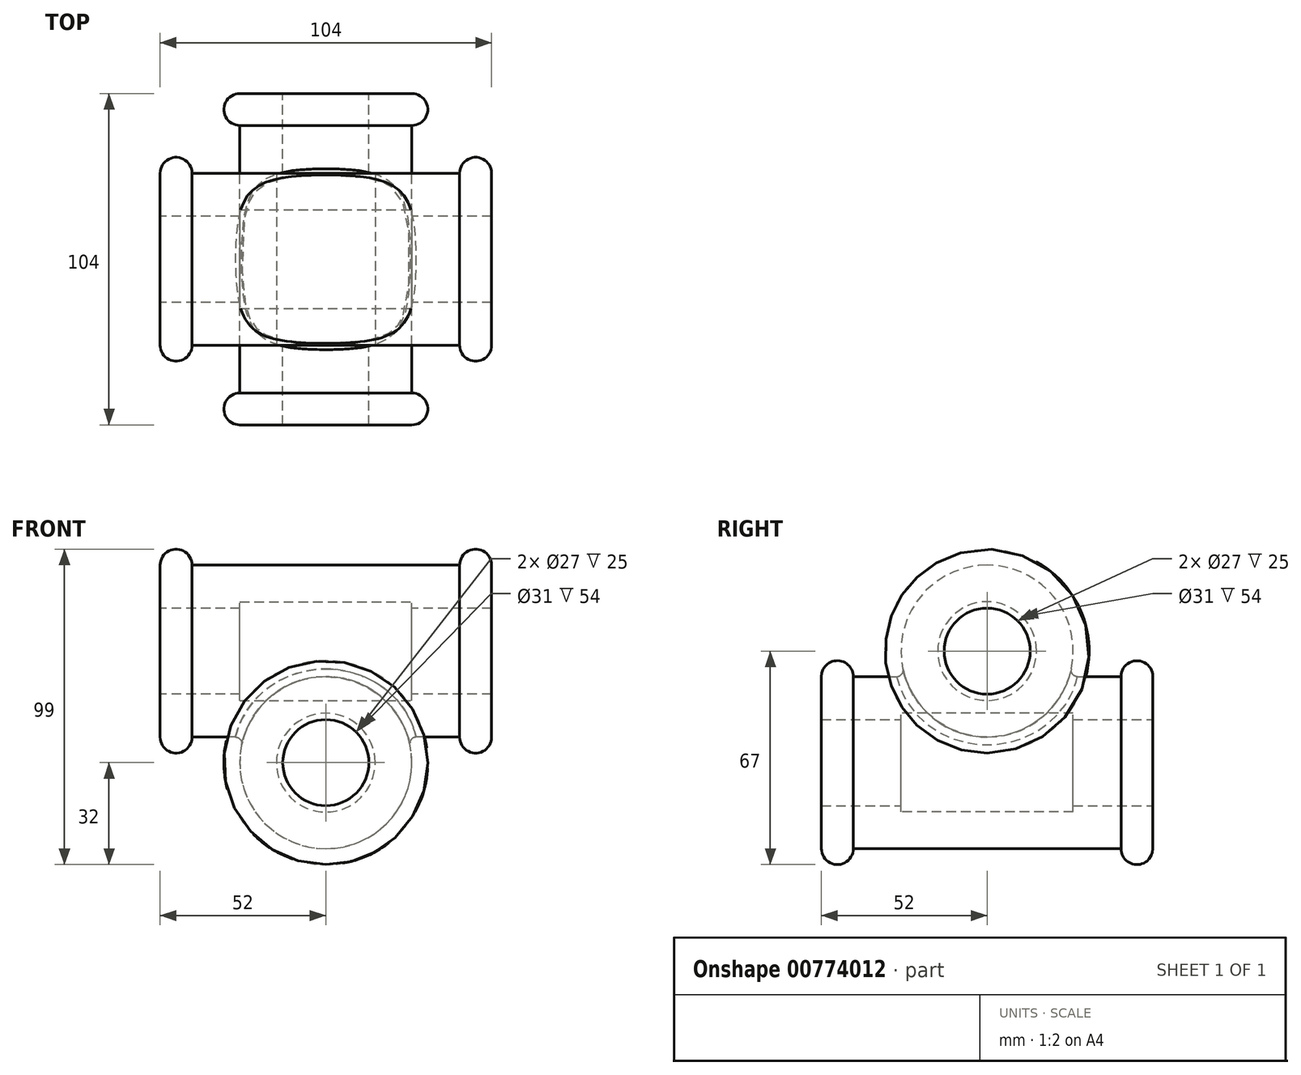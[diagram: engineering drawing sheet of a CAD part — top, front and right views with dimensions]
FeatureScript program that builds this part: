
annotation { "Feature Type Name" : "Feature", "Feature Type Description" : "" }
export const myFeature = defineFeature(function(context is Context, id is Id, definition is map)
    precondition{}
    {
        {
            var Q0;
            Q0=qCreatedBy(makeId("Front.planeOp"),FACE);
            var sketch = newSketch(context, id + "F0", { "sketchPlane" : qUnion([Q0])});
            skCircle(sketch, "E0", {"center": v(0, 0) * mm, "radius": 13.5 * mm});
            skCircle(sketch, "E1", {"center": v(0, 0) * mm, "radius": 15.5 * mm});
            skCircle(sketch, "E2", {"center": v(0, 0) * mm, "radius": 27 * mm});
            skSolve(sketch);
        }
        {
            var Q0;
            Q0 = qSketchRegion(id + "F0", true);
            var Q1;
            Q1=makeQuery(id+"F0.imprint","IMPRINT",FACE,{"disambiguationData":[TD([[makeQuery(id+"F0.imprint","IMPRINT",EDGE,{"derivedFrom":sQuery(id+"F0.wireOp",EDGE,"E0")}),-1.0]])]});
            extrude(context, id + "F1", {"entities" : qUnion([Q0, Q1]), "depth" : 104 * mm, "offsetDistance" : 25 * mm, "symmetric" : true});
        }
        {
            var Q0;
            Q0=makeQuery(id+"F1.opExtrude","CAP_FACE",FACE,{"disambiguationData":[OSD([sQuery(id+"F0.wireOp",EDGE,"E0"),sQuery(id+"F0.wireOp",EDGE,"E2")])],"isStart":true});
            var sketch = newSketch(context, id + "F2", { "sketchPlane" : qUnion([Q0])});
            skCircle(sketch, "E3", {"center": v(0, 0) * mm, "radius": 32 * mm});
            skSolve(sketch);
        }
        {
            var Q0;
            Q0=makeQuery(id+"F2.imprint","IMPRINT",FACE,{"disambiguationData":[TD([[makeQuery(id+"F2.imprint","IMPRINT",EDGE,{"derivedFrom":sQuery(id+"F2.wireOp",EDGE,"E3")}),1.0]])]});
            extrude(context, id + "F3", {"entities" : qUnion([Q0]), "operationType" : NewBodyOperationType.ADD, "oppositeDirection" : true, "depth" : 10 * mm, "offsetDistance" : 25 * mm});
        }
        {
            var Q0;
            Q0=makeQuery(id+"F1.opExtrude","CAP_FACE",FACE,{"disambiguationData":[OSD([sQuery(id+"F0.wireOp",EDGE,"E0"),sQuery(id+"F0.wireOp",EDGE,"E2")])],"isStart":false});
            var sketch = newSketch(context, id + "F4", { "sketchPlane" : qUnion([Q0])});
            skCircle(sketch, "E4", {"center": v(0, 0) * mm, "radius": 32 * mm});
            skCircle(sketch, "E5", {"center": v(0, 0) * mm, "radius": 13.5 * mm});
            skSolve(sketch);
        }
        {
            var Q0;
            Q0=makeQuery(id+"F4.imprint","IMPRINT",FACE,{"disambiguationData":[TD([[makeQuery(id+"F4.imprint","IMPRINT",EDGE,{"derivedFrom":sQuery(id+"F4.wireOp",EDGE,"E4")}),1.0]])]});
            var Q1;
            Q1=makeQuery(id+"F4.imprint","IMPRINT",FACE,{"disambiguationData":[TD([[makeQuery(id+"F4.imprint","IMPRINT",EDGE,{"derivedFrom":makeQuery(id+"F1.opExtrude","CAP_EDGE",EDGE,{"disambiguationData":[OSD([sQuery(id+"F0.wireOp",EDGE,"E0")])],"isStart":false})}),1.0]])]});
            extrude(context, id + "F5", {"entities" : qUnion([Q0, Q1]), "operationType" : NewBodyOperationType.ADD, "oppositeDirection" : true, "depth" : 10 * mm, "offsetDistance" : 25 * mm});
        }
        {
            var Q0;
            Q0=makeQuery(id+"F3.opExtrude","CAP_EDGE",EDGE,{"disambiguationData":[OSD([sQuery(id+"F2.wireOp",EDGE,"E3")])],"isStart":false});
            var Q1;
            Q1=makeQuery(id+"F5.opExtrude","CAP_EDGE",EDGE,{"disambiguationData":[OSD([sQuery(id+"F4.wireOp",EDGE,"E4")])],"isStart":false});
            var Q2;
            Q2=makeQuery(id+"F5.opExtrude","CAP_EDGE",EDGE,{"disambiguationData":[OSD([sQuery(id+"F4.wireOp",EDGE,"E4")])],"isStart":true});
            var Q3;
            Q3=makeQuery(id+"F3.opExtrude","CAP_EDGE",EDGE,{"disambiguationData":[OSD([sQuery(id+"F2.wireOp",EDGE,"E3")])],"isStart":true});
            fillet(context, id + "F6", {"entities" : qUnion([Q0, Q1, Q2, Q3]), "radius" : 5 * mm, "tangentPropagation" : true, "allowEdgeOverflow" : false});
        }
        {
            var Q0;
            Q0=qCreatedBy(makeId("Right.planeOp"),FACE);
            var sketch = newSketch(context, id + "F7", { "sketchPlane" : qUnion([Q0])});
            skCircle(sketch, "E6", {"center": v(0, 35) * mm, "radius": 13.5 * mm});
            skCircle(sketch, "E7", {"center": v(0, 35) * mm, "radius": 15.5 * mm});
            skCircle(sketch, "E8", {"center": v(0, 35) * mm, "radius": 27 * mm});
            skLineSegment(sketch, "E9", {"start": v(0, 0) * mm, "end": v(0, 35) * mm, "construction": true});
            skSolve(sketch);
        }
        {
            var Q0;
            Q0 = qSketchRegion(id + "F7", true);
            var Q1;
            Q1=makeQuery(id+"F7.imprint","IMPRINT",FACE,{"disambiguationData":[TD([[makeQuery(id+"F7.imprint","IMPRINT",EDGE,{"derivedFrom":sQuery(id+"F7.wireOp",EDGE,"E6")}),-1.0]])]});
            extrude(context, id + "F8", {"entities" : qUnion([Q0, Q1]), "operationType" : NewBodyOperationType.ADD, "depth" : 104 * mm, "offsetDistance" : 25 * mm, "symmetric" : true});
        }
        {
            var Q0;
            Q0=makeQuery(id+"F8.opExtrude","CAP_FACE",FACE,{"disambiguationData":[OSD([sQuery(id+"F7.wireOp",EDGE,"E6"),sQuery(id+"F7.wireOp",EDGE,"E8")])],"isStart":true});
            var sketch = newSketch(context, id + "F9", { "sketchPlane" : qUnion([Q0])});
            skCircle(sketch, "E10", {"center": v(0, 35) * mm, "radius": 32 * mm});
            skCircle(sketch, "E11", {"center": v(0, 35) * mm, "radius": 13.5 * mm});
            skSolve(sketch);
        }
        {
            var Q0;
            Q0 = qSketchRegion(id + "F9", true);
            extrude(context, id + "F10", {"entities" : qUnion([Q0]), "operationType" : NewBodyOperationType.ADD, "oppositeDirection" : true, "depth" : 10 * mm, "offsetDistance" : 25 * mm});
        }
        {
            var Q0;
            Q0=makeQuery(id+"F8.opExtrude","CAP_FACE",FACE,{"disambiguationData":[OSD([sQuery(id+"F7.wireOp",EDGE,"E6"),sQuery(id+"F7.wireOp",EDGE,"E8")])],"isStart":false});
            var sketch = newSketch(context, id + "F11", { "sketchPlane" : qUnion([Q0])});
            skCircle(sketch, "E12", {"center": v(0, 35) * mm, "radius": 32 * mm});
            skCircle(sketch, "E13", {"center": v(0, 35) * mm, "radius": 13.5 * mm});
            skSolve(sketch);
        }
        {
            var Q0;
            Q0 = qSketchRegion(id + "F11", true);
            extrude(context, id + "F12", {"entities" : qUnion([Q0]), "operationType" : NewBodyOperationType.ADD, "oppositeDirection" : true, "depth" : 10 * mm, "offsetDistance" : 25 * mm});
        }
        {
            var Q0;
            Q0=makeQuery(id+"F0.imprint","IMPRINT",FACE,{"disambiguationData":[TD([[makeQuery(id+"F0.imprint","IMPRINT",EDGE,{"derivedFrom":sQuery(id+"F0.wireOp",EDGE,"E0")}),-1.0]])]});
            var Q1;
            Q1=makeQuery(id+"F0.imprint","IMPRINT",FACE,{"disambiguationData":[TD([[makeQuery(id+"F0.imprint","IMPRINT",EDGE,{"derivedFrom":sQuery(id+"F0.wireOp",EDGE,"E0")}),1.0]])]});
            extrude(context, id + "F13", {"entities" : qUnion([Q0, Q1]), "operationType" : NewBodyOperationType.REMOVE, "oppositeDirection" : true, "depth" : 54 * mm, "offsetDistance" : 25 * mm, "symmetric" : true});
        }
        {
            var Q0;
            Q0=makeQuery(id+"F12.opExtrude","CAP_EDGE",EDGE,{"disambiguationData":[OSD([sQuery(id+"F11.wireOp",EDGE,"E12")])],"isStart":true});
            var Q1;
            Q1=makeQuery(id+"F12.opExtrude","CAP_EDGE",EDGE,{"disambiguationData":[OSD([sQuery(id+"F11.wireOp",EDGE,"E12")])],"isStart":false});
            var Q2;
            Q2=makeQuery(id+"F10.opExtrude","CAP_EDGE",EDGE,{"disambiguationData":[OSD([sQuery(id+"F9.wireOp",EDGE,"E10")])],"isStart":true});
            var Q3;
            Q3=makeQuery(id+"F10.opExtrude","CAP_EDGE",EDGE,{"disambiguationData":[OSD([sQuery(id+"F9.wireOp",EDGE,"E10")])],"isStart":false});
            fillet(context, id + "F14", {"entities" : qUnion([Q0, Q1, Q2, Q3]), "radius" : 5 * mm, "tangentPropagation" : true, "allowEdgeOverflow" : false});
        }
        {
            var Q0;
            Q0=makeQuery(id+"F7.imprint","IMPRINT",FACE,{"disambiguationData":[TD([[makeQuery(id+"F7.imprint","IMPRINT",EDGE,{"derivedFrom":sQuery(id+"F7.wireOp",EDGE,"E6")}),-1.0]])]});
            var Q1;
            Q1=makeQuery(id+"F7.imprint","IMPRINT",FACE,{"disambiguationData":[TD([[makeQuery(id+"F7.imprint","IMPRINT",EDGE,{"derivedFrom":sQuery(id+"F7.wireOp",EDGE,"E6")}),1.0]])]});
            extrude(context, id + "F15", {"entities" : qUnion([Q0, Q1]), "operationType" : NewBodyOperationType.REMOVE, "oppositeDirection" : true, "depth" : 54 * mm, "offsetDistance" : 25 * mm, "symmetric" : true});
        }
        {
            var Q0;
            Q0=makeQuery(id+"F8.boolean.opBoolean","INTERSECT",EDGE,{"derivedFrom":[makeQuery(id+"F1.opExtrude","SWEPT_FACE",FACE,{"disambiguationData":[OSD([sQuery(id+"F0.wireOp",EDGE,"E2")])]}),makeQuery(id+"F8.opExtrude","SWEPT_FACE",FACE,{"disambiguationData":[OSD([sQuery(id+"F7.wireOp",EDGE,"E8")])]})]});
            fillet(context, id + "F16", {"entities" : qUnion([Q0]), "radius" : 2 * mm, "tangentPropagation" : true, "allowEdgeOverflow" : false});
        }
    });
